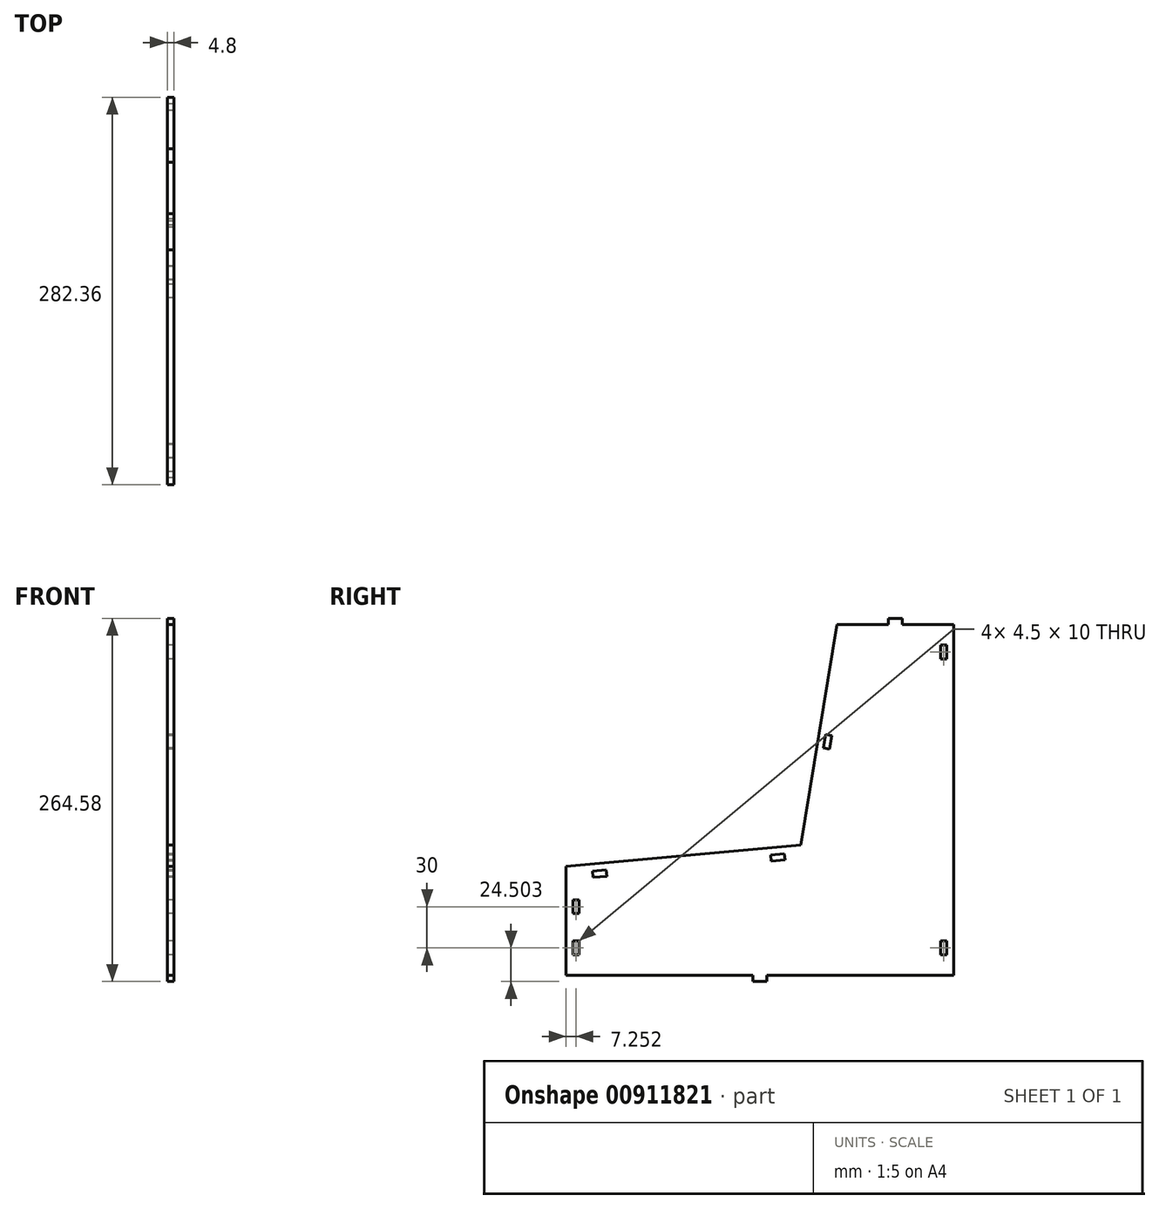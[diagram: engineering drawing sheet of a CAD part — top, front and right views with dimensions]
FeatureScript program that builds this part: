
annotation { "Feature Type Name" : "Feature", "Feature Type Description" : "" }
export const myFeature = defineFeature(function(context is Context, id is Id, definition is map)
    precondition{}
    {
        {
            var Q0;
            Q0=qCreatedBy(makeId("Right.planeOp"),FACE);
            var sketch = newSketch(context, id + "F0", { "sketchPlane" : qUnion([Q0])});
            skLineSegment(sketch, "E0", {"start": v(-803.7, 329.08) * mm, "end": v(-803.7, 344.08) * mm});
            skLineSegment(sketch, "E1", {"start": v(-803.7, 399.08) * mm, "end": v(-788.96, 400.44) * mm});
            skLineSegment(sketch, "E2", {"start": v(-634.23, 414.66) * mm, "end": v(-606.22, 584.66) * mm});
            skLineSegment(sketch, "E3", {"start": v(-606.22, 584.66) * mm, "end": v(-531.34, 584.66) * mm});
            skLineSegment(sketch, "E4", {"start": v(-788.96, 400.44) * mm, "end": v(-789.37, 404.92) * mm});
            skLineSegment(sketch, "E5", {"start": v(-779.4, 405.84) * mm, "end": v(-779, 401.35) * mm});
            skLineSegment(sketch, "E6", {"start": v(-634.23, 414.66) * mm, "end": v(-649.16, 413.3) * mm});
            skLineSegment(sketch, "E7", {"start": v(-649.16, 413.3) * mm, "end": v(-649.58, 417.77) * mm});
            skLineSegment(sketch, "E8", {"start": v(-659.53, 416.86) * mm, "end": v(-659.12, 412.37) * mm});
            skLineSegment(sketch, "E9.trimOffspring", {"start": v(-779, 401.35) * mm, "end": v(-659.12, 412.37) * mm});
            skLineSegment(sketch, "E10.trimOffspring", {"start": v(-649.16, 413.3) * mm, "end": v(-634.23, 414.66) * mm});
            skLineSegment(sketch, "E11", {"start": v(-803.7, 399.08) * mm, "end": v(-803.7, 384.08) * mm});
            skLineSegment(sketch, "E12", {"start": v(-803.7, 384.08) * mm, "end": v(-799.2, 384.08) * mm});
            skLineSegment(sketch, "E13", {"start": v(-799.2, 384.08) * mm, "end": v(-799.2, 374.08) * mm});
            skLineSegment(sketch, "E14", {"start": v(-799.2, 374.08) * mm, "end": v(-803.7, 374.08) * mm});
            skLineSegment(sketch, "E15.MirrorCS", {"start": v(-799.2, 354.08) * mm, "end": v(-803.7, 354.08) * mm});
            skLineSegment(sketch, "E16.MirrorCS", {"start": v(-803.7, 344.08) * mm, "end": v(-799.2, 344.08) * mm});
            skLineSegment(sketch, "E17.trimOffspring", {"start": v(-803.7, 384.08) * mm, "end": v(-803.7, 399.08) * mm});
            skLineSegment(sketch, "E18.trimOffspring", {"start": v(-803.7, 354.08) * mm, "end": v(-803.7, 374.08) * mm});
            skLineSegment(sketch, "E19", {"start": v(-531.34, 584.66) * mm, "end": v(-531.34, 329.08) * mm});
            skLineSegment(sketch, "E20", {"start": v(-531.34, 569.66) * mm, "end": v(-535.84, 569.66) * mm});
            skLineSegment(sketch, "E21", {"start": v(-535.84, 569.66) * mm, "end": v(-535.84, 559.66) * mm});
            skLineSegment(sketch, "E22", {"start": v(-535.84, 559.66) * mm, "end": v(-531.34, 559.66) * mm});
            skLineSegment(sketch, "E23.MirrorCS", {"start": v(-535.84, 354.08) * mm, "end": v(-531.34, 354.08) * mm});
            skLineSegment(sketch, "E24.MirrorCS", {"start": v(-531.34, 344.08) * mm, "end": v(-535.84, 344.08) * mm});
            skLineSegment(sketch, "E25", {"start": v(-531.34, 329.08) * mm, "end": v(-662.52, 329.08) * mm});
            skLineSegment(sketch, "E26", {"start": v(-672.52, 329.08) * mm, "end": v(-672.52, 324.58) * mm});
            skLineSegment(sketch, "E27.MirrorCS", {"start": v(-662.52, 329.08) * mm, "end": v(-662.52, 324.58) * mm});
            skPoint(sketch, "E28.end.orphan", {"position": v(-667.52, 329.08) * mm});
            skLineSegment(sketch, "E29.trimOffspring", {"start": v(-672.52, 329.08) * mm, "end": v(-803.7, 329.08) * mm});
            skLineSegment(sketch, "E30", {"start": v(-568.78, 584.66) * mm, "end": v(-568.78, 589.16) * mm});
            skLineSegment(sketch, "E31", {"start": v(-568.78, 589.16) * mm, "end": v(-573.78, 589.16) * mm});
            skLineSegment(sketch, "E32", {"start": v(-573.78, 589.16) * mm, "end": v(-573.78, 584.66) * mm});
            skLineSegment(sketch, "E33.MirrorCS", {"start": v(-568.78, 589.16) * mm, "end": v(-563.78, 589.16) * mm});
            skLineSegment(sketch, "E34.MirrorCS", {"start": v(-563.78, 589.16) * mm, "end": v(-563.78, 584.66) * mm});
            skLineSegment(sketch, "E35", {"start": v(-620.22, 499.66) * mm, "end": v(-615.78, 498.93) * mm});
            skLineSegment(sketch, "E36", {"start": v(-615.78, 498.93) * mm, "end": v(-614.97, 503.87) * mm});
            skLineSegment(sketch, "E37", {"start": v(-614.97, 503.87) * mm, "end": v(-619.41, 504.6) * mm});
            skLineSegment(sketch, "E38.MirrorCS", {"start": v(-615.78, 498.93) * mm, "end": v(-616.6, 494) * mm});
            skLineSegment(sketch, "E39.MirrorCS", {"start": v(-616.6, 494) * mm, "end": v(-621.04, 494.73) * mm});
            skLineSegment(sketch, "E40", {"start": v(-526.34, 584.66) * mm, "end": v(-526.34, 329.08) * mm});
            skLineSegment(sketch, "E41.0", {"start": v(-808.7, 354.08) * mm, "end": v(-808.7, 374.08) * mm});
            skLineSegment(sketch, "E42", {"start": v(-803.7, 384.08) * mm, "end": v(-803.7, 344.08) * mm});
            skLineSegment(sketch, "E43", {"start": v(-808.7, 374.08) * mm, "end": v(-808.7, 399.08) * mm});
            skLineSegment(sketch, "E44", {"start": v(-808.7, 399.08) * mm, "end": v(-803.7, 399.08) * mm});
            skLineSegment(sketch, "E45", {"start": v(-808.7, 354.08) * mm, "end": v(-808.7, 329.08) * mm});
            skLineSegment(sketch, "E46", {"start": v(-808.7, 329.08) * mm, "end": v(-803.7, 329.08) * mm});
            skLineSegment(sketch, "E47", {"start": v(-531.34, 329.08) * mm, "end": v(-526.34, 329.08) * mm});
            skLineSegment(sketch, "E48", {"start": v(-531.34, 584.66) * mm, "end": v(-526.34, 584.66) * mm});
            skLineSegment(sketch, "E49", {"start": v(-611.29, 584.66) * mm, "end": v(-639.37, 414.2) * mm});
            skLineSegment(sketch, "E50", {"start": v(-611.29, 584.66) * mm, "end": v(-606.22, 584.66) * mm});
            skLineSegment(sketch, "E51", {"start": v(-808.7, 399.08) * mm, "end": v(-808.7, 403.44) * mm});
            skLineSegment(sketch, "E52", {"start": v(-650.06, 423.05) * mm, "end": v(-637.73, 424.18) * mm});
            skLineSegment(sketch, "E53", {"start": v(-637.73, 424.18) * mm, "end": v(-808.7, 408.46) * mm});
            skLineSegment(sketch, "E54", {"start": v(-808.7, 403.44) * mm, "end": v(-808.7, 408.46) * mm});
            skLineSegment(sketch, "E55", {"start": v(-788.96, 400.44) * mm, "end": v(-779, 401.35) * mm});
            skLineSegment(sketch, "E56", {"start": v(-659.12, 412.37) * mm, "end": v(-649.16, 413.3) * mm});
            skLineSegment(sketch, "E57", {"start": v(-789.37, 404.92) * mm, "end": v(-779.4, 405.84) * mm});
            skLineSegment(sketch, "E58", {"start": v(-799.2, 354.08) * mm, "end": v(-799.2, 344.08) * mm});
            skPoint(sketch, "E59.orphan", {"position": v(-798.9, 344.08) * mm});
            skLineSegment(sketch, "E60", {"start": v(-659.53, 416.86) * mm, "end": v(-649.58, 417.77) * mm});
            skLineSegment(sketch, "E61", {"start": v(-662.52, 324.58) * mm, "end": v(-672.52, 324.58) * mm});
            skPoint(sketch, "E62.end.orphan", {"position": v(-667.52, 324.28) * mm});
            skPoint(sketch, "E63.orphan", {"position": v(-672.52, 324.28) * mm});
            skLineSegment(sketch, "E64", {"start": v(-535.84, 354.1) * mm, "end": v(-535.84, 344.08) * mm});
            skSolve(sketch);
        }
        {
            var Q0;
            Q0=makeQuery(id+"F0.imprint","IMPRINT",FACE,{"disambiguationData":[TD([[makeQuery(id+"F0.imprint","IMPRINT",EDGE,{"derivedFrom":sQuery(id+"F0.wireOp",EDGE,"8uoMc77t-Hmir-v5Bd-Xkfh-7KWAXlDmngZL")}),1.0]])]});
            var Q1;
            Q1=makeQuery(id+"F0.imprint","IMPRINT",FACE,{"disambiguationData":[TD([[makeQuery(id+"F0.imprint","IMPRINT",EDGE,{"derivedFrom":sQuery(id+"F0.wireOp",EDGE,"cDMpMdSZ-OzRD-cC9o-GCdK-vFHv1NvtsfW1")}),-1.0]])]});
            var Q2;
            {var subQ0=sQuery(id+"F0.wireOp",EDGE,"qpHv3P1K-Quo5-HdHm-u7b5-UL0i1nFsk6MX");Q2=makeQuery(id+"F0.imprint","IMPRINT",FACE,{"disambiguationData":[TD([[makeQuery(id+"F0.imprint","IMPRINT",EDGE,{"derivedFrom":subQ0}),-1.0]])]});}
            var Q3;
            {var subQ0=sQuery(id+"F0.wireOp",EDGE,"qpHv3P1K-Quo5-HdHm-u7b5-UL0i1nFsk6MX");Q3=makeQuery(id+"F0.imprint","IMPRINT",FACE,{"disambiguationData":[TD([[makeQuery(id+"F0.imprint","IMPRINT",EDGE,{"derivedFrom":subQ0}),1.0]])]});}
            var Q4;
            Q4=makeQuery(id+"F0.imprint","IMPRINT",FACE,{"disambiguationData":[TD([[makeQuery(id+"F0.imprint","IMPRINT",EDGE,{"derivedFrom":sQuery(id+"F0.wireOp",EDGE,"E40")}),-1.0]])]});
            var Q5;
            {var subQ7=sQuery(id+"F0.wireOp",EDGE,"E49");Q5=makeQuery(id+"F0.imprint","IMPRINT",FACE,{"disambiguationData":[TD([[makeQuery(id+"F0.imprint","IMPRINT",EDGE,{"derivedFrom":subQ7}),1.0]])]});}
            var Q6;
            Q6=makeQuery(id+"F0.imprint","IMPRINT",FACE,{"disambiguationData":[TD([[makeQuery(id+"F0.imprint","IMPRINT",EDGE,{"derivedFrom":sQuery(id+"F0.wireOp",EDGE,"E0")}),-1.0]])]});
            var Q7;
            {var subQ3=sQuery(id+"F0.wireOp",EDGE,"E0");Q7=makeQuery(id+"F0.imprint","IMPRINT",FACE,{"disambiguationData":[TD([[makeQuery(id+"F0.imprint","IMPRINT",EDGE,{"derivedFrom":subQ3}),1.0]])]});}
            var Q8;
            {var subQ0=sQuery(id+"F0.wireOp",EDGE,"E5");Q8=makeQuery(id+"F0.imprint","IMPRINT",FACE,{"disambiguationData":[TD([[makeQuery(id+"F0.imprint","IMPRINT",EDGE,{"derivedFrom":subQ0}),1.0]])]});}
            var Q9;
            {var subQ0=sQuery(id+"F0.wireOp",EDGE,"E7");Q9=makeQuery(id+"F0.imprint","IMPRINT",FACE,{"disambiguationData":[TD([[makeQuery(id+"F0.imprint","IMPRINT",EDGE,{"derivedFrom":subQ0}),-1.0]])]});}
            var Q10;
            Q10=makeQuery(id+"F0.imprint","IMPRINT",FACE,{"disambiguationData":[TD([[makeQuery(id+"F0.imprint","IMPRINT",EDGE,{"derivedFrom":sQuery(id+"F0.wireOp",EDGE,"E1")}),1.0]])]});
            var Q11;
            {var subQ0=sQuery(id+"F0.wireOp",EDGE,"E30");Q11=makeQuery(id+"F0.imprint","IMPRINT",FACE,{"disambiguationData":[TD([[makeQuery(id+"F0.imprint","IMPRINT",EDGE,{"derivedFrom":subQ0}),-1.0]])]});}
            var Q12;
            {var subQ0=sQuery(id+"F0.wireOp",EDGE,"E30");Q12=makeQuery(id+"F0.imprint","IMPRINT",FACE,{"disambiguationData":[TD([[makeQuery(id+"F0.imprint","IMPRINT",EDGE,{"derivedFrom":subQ0}),1.0]])]});}
            extrude(context, id + "F1", {"entities" : qUnion([Q0, Q1, Q2, Q3, Q4, Q5, Q6, Q7, Q8, Q9, Q10, Q11, Q12]), "depth" : 4.8 * mm, "offsetDistance" : 25 * mm});
        }
    });
